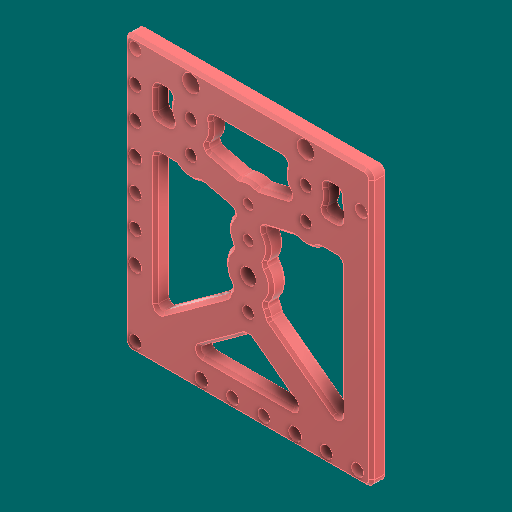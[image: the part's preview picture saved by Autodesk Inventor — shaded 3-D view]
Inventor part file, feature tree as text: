
AUTODESK INVENTOR PART (.ipt)
format: ipt  version: 2023.1 (Build 271208000, 208)  size: 542,208 bytes
history: native  units: in
note: dims shown in document units (in); Inventor stores cm internally (conversion verified against a paired STEP export)
features: other x3, sketch x2
ambient origin geometry x8: Origin, YZ Plane, XZ Plane, XY Plane, X Axis, Y Axis, Z Axis, Center Point
bodies: Solid1 (feature_tree)
feature tree (5):
  other  "TopPlate.ipt"
  other  "Solid1::TopPlate.ipt"
  other  "TaggingFeature1"
  sketch  "Sketch1"  dims[d0=0.3937in]
  sketch  "Sketch2"
